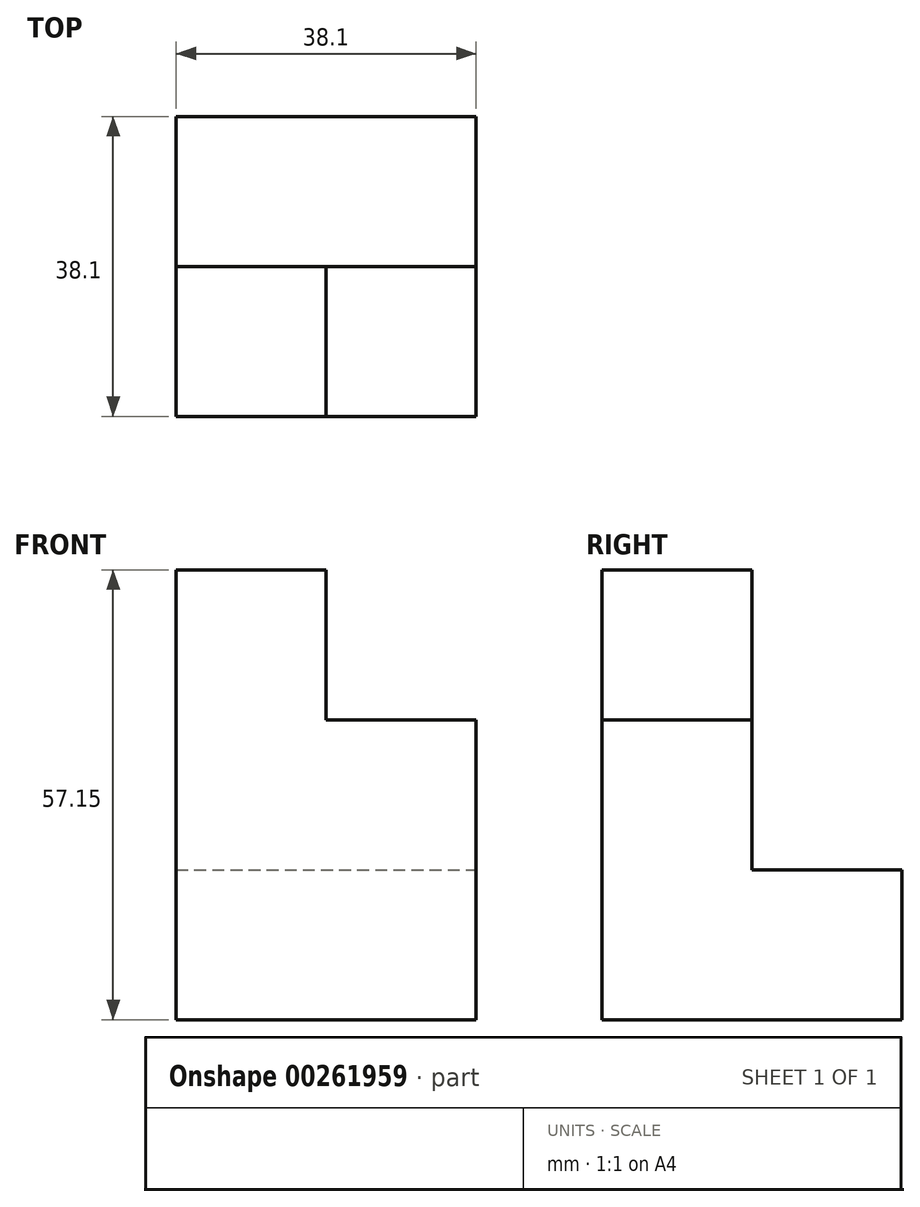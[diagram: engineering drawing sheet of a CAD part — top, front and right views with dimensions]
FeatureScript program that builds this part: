
annotation { "Feature Type Name" : "Feature", "Feature Type Description" : "" }
export const myFeature = defineFeature(function(context is Context, id is Id, definition is map)
    precondition{}
    {
        {
            var Q0;
            Q0=qCreatedBy(makeId("Front.planeOp"),FACE);
            var sketch = newSketch(context, id + "F0", { "sketchPlane" : qUnion([Q0])});
            skLineSegment(sketch, "E0.bottom", {"start": v(0, 0) * mm, "end": v(19.05, 0) * mm});
            skLineSegment(sketch, "E0.top", {"start": v(0, -19.05) * mm, "end": v(19.05, -19.05) * mm});
            skLineSegment(sketch, "E0.left", {"start": v(0, 0) * mm, "end": v(0, -19.05) * mm});
            skLineSegment(sketch, "E0.right", {"start": v(19.05, 0) * mm, "end": v(19.05, -19.05) * mm});
            skLineSegment(sketch, "E1.MirrorCS", {"start": v(0, 0) * mm, "end": v(0, 19.05) * mm});
            skLineSegment(sketch, "E2.MirrorCS", {"start": v(0, 19.05) * mm, "end": v(19.05, 19.05) * mm});
            skLineSegment(sketch, "E3.MirrorCS", {"start": v(19.05, 0) * mm, "end": v(19.05, 19.05) * mm});
            skLineSegment(sketch, "E4.MirrorCS", {"start": v(0, 38.1) * mm, "end": v(0, 19.05) * mm});
            skLineSegment(sketch, "E5.MirrorCS", {"start": v(0, 38.1) * mm, "end": v(19.05, 38.1) * mm});
            skLineSegment(sketch, "E6.MirrorCS", {"start": v(19.05, 38.1) * mm, "end": v(19.05, 19.05) * mm});
            skLineSegment(sketch, "E7.MirrorCS", {"start": v(38.1, 19.05) * mm, "end": v(19.05, 19.05) * mm});
            skLineSegment(sketch, "E8.MirrorCS", {"start": v(38.1, 0) * mm, "end": v(38.1, 19.05) * mm});
            skLineSegment(sketch, "E9.MirrorCS", {"start": v(38.1, 0) * mm, "end": v(19.05, 0) * mm});
            skLineSegment(sketch, "E10.MirrorCS", {"start": v(38.1, 0) * mm, "end": v(38.1, -19.05) * mm});
            skLineSegment(sketch, "E11.MirrorCS", {"start": v(38.1, -19.05) * mm, "end": v(19.05, -19.05) * mm});
            skSolve(sketch);
        }
        {
            var Q0;
            Q0 = qSketchRegion(id + "F0", true);
            extrude(context, id + "F1", {"entities" : qUnion([Q0]), "depth" : 19.05 * mm});
        }
        {
            var Q0;
            Q0=qCreatedBy(makeId("Front.planeOp"),FACE);
            var sketch = newSketch(context, id + "F2", { "sketchPlane" : qUnion([Q0])});
            skLineSegment(sketch, "E12.bottom", {"start": v(0, 0) * mm, "end": v(19.05, 0) * mm});
            skLineSegment(sketch, "E12.top", {"start": v(0, -19.05) * mm, "end": v(19.05, -19.05) * mm});
            skLineSegment(sketch, "E12.left", {"start": v(0, 0) * mm, "end": v(0, -19.05) * mm});
            skLineSegment(sketch, "E12.right", {"start": v(19.05, 0) * mm, "end": v(19.05, -19.05) * mm});
            skSolve(sketch);
        }
        {
            var Q0;
            Q0=makeQuery(id+"F2.imprint","IMPRINT",FACE,{"disambiguationData":[TD([[makeQuery(id+"F2.imprint","IMPRINT",EDGE,{"derivedFrom":sQuery(id+"F2.wireOp",EDGE,"E12.bottom")}),-1.0]])]});
            extrude(context, id + "F3", {"entities" : qUnion([Q0]), "operationType" : NewBodyOperationType.ADD, "oppositeDirection" : true, "depth" : 19.05 * mm});
        }
        {
            var Q0;
            Q0=makeQuery(id+"F3.opExtrude","SWEPT_FACE",FACE,{"disambiguationData":[OSD([sQuery(id+"F2.wireOp",EDGE,"E12.right")])]});
            extrude(context, id + "F4", {"entities" : qUnion([Q0]), "operationType" : NewBodyOperationType.ADD, "depth" : 19.05 * mm});
        }
    });
